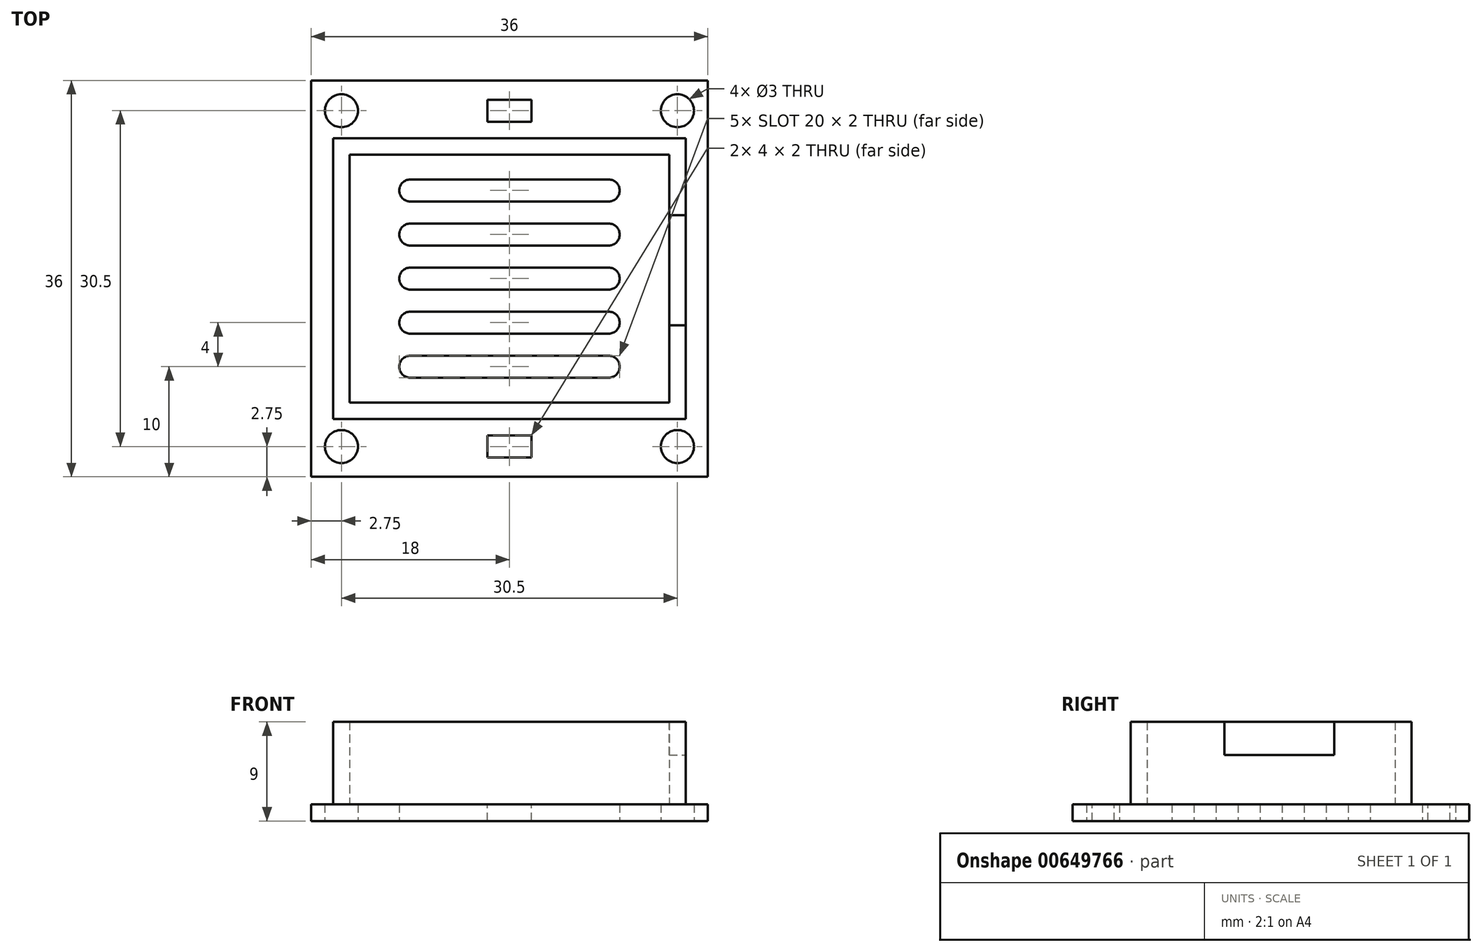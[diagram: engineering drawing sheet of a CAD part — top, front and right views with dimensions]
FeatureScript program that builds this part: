
annotation { "Feature Type Name" : "Feature", "Feature Type Description" : "" }
export const myFeature = defineFeature(function(context is Context, id is Id, definition is map)
    precondition{}
    {
        {
            var Q0;
            Q0=qCreatedBy(makeId("Top.planeOp"),FACE);
            var sketch = newSketch(context, id + "F0", { "sketchPlane" : qUnion([Q0])});
            skLineSegment(sketch, "E0.bottom", {"start": v(18, 18) * mm, "end": v(-18, 18) * mm});
            skLineSegment(sketch, "E0.top", {"start": v(18, -18) * mm, "end": v(-18, -18) * mm});
            skLineSegment(sketch, "E0.left", {"start": v(18, 18) * mm, "end": v(18, -18) * mm});
            skLineSegment(sketch, "E0.right", {"start": v(-18, 18) * mm, "end": v(-18, -18) * mm});
            skLineSegment(sketch, "E1.bottom", {"start": v(15.25, 15.25) * mm, "end": v(-15.25, 15.25) * mm, "construction": true});
            skLineSegment(sketch, "E1.top", {"start": v(15.25, -15.25) * mm, "end": v(-15.25, -15.25) * mm, "construction": true});
            skLineSegment(sketch, "E1.left", {"start": v(15.25, 15.25) * mm, "end": v(15.25, -15.25) * mm, "construction": true});
            skLineSegment(sketch, "E1.right", {"start": v(-15.25, 15.25) * mm, "end": v(-15.25, -15.25) * mm, "construction": true});
            skCircle(sketch, "E2", {"center": v(-15.25, 15.25) * mm, "radius": 1.5 * mm});
            skCircle(sketch, "E3", {"center": v(15.25, 15.25) * mm, "radius": 1.5 * mm});
            skCircle(sketch, "E4", {"center": v(15.25, -15.25) * mm, "radius": 1.5 * mm});
            skCircle(sketch, "E5", {"center": v(-15.25, -15.25) * mm, "radius": 1.5 * mm});
            skPoint(sketch, "E6.centerSnap0", {"position": v(15.25, 0) * mm});
            skSolve(sketch);
        }
        {
            var Q0;
            Q0=qCreatedBy(makeId("Top.planeOp"),FACE);
            var sketch = newSketch(context, id + "F1", { "sketchPlane" : qUnion([Q0])});
            skPoint(sketch, "E7.middle", {"position": v(0, 0) * mm});
            skLineSegment(sketch, "E8.bottom", {"start": v(-14.5, 11.25) * mm, "end": v(14.5, 11.25) * mm, "construction": true});
            skLineSegment(sketch, "E8.top", {"start": v(-14.5, -11.25) * mm, "end": v(14.5, -11.25) * mm, "construction": true});
            skLineSegment(sketch, "E8.left", {"start": v(-14.5, 11.25) * mm, "end": v(-14.5, -11.25) * mm, "construction": true});
            skLineSegment(sketch, "E8.right", {"start": v(14.5, 11.25) * mm, "end": v(14.5, -11.25) * mm, "construction": true});
            skLineSegment(sketch, "E9.bottom", {"start": v(-16, 12.75) * mm, "end": v(16, 12.75) * mm});
            skLineSegment(sketch, "E9.top", {"start": v(-16, -12.75) * mm, "end": v(16, -12.75) * mm});
            skLineSegment(sketch, "E9.left", {"start": v(-16, 12.75) * mm, "end": v(-16, -12.75) * mm});
            skLineSegment(sketch, "E9.right", {"start": v(16, 12.75) * mm, "end": v(16, -12.75) * mm});
            skSolve(sketch);
        }
        {
            var Q0;
            Q0=qCreatedBy(makeId("Top.planeOp"),FACE);
            var sketch = newSketch(context, id + "F2", { "sketchPlane" : qUnion([Q0])});
            skLineSegment(sketch, "E10.bottom", {"start": v(-9, 1) * mm, "end": v(9, 1) * mm});
            skLineSegment(sketch, "E10.top", {"start": v(-9, -1) * mm, "end": v(9, -1) * mm});
            skLineSegment(sketch, "E10.left", {"start": v(-9, 1) * mm, "end": v(-9, -1) * mm});
            skLineSegment(sketch, "E10.right", {"start": v(9, 1) * mm, "end": v(9, -1) * mm});
            skPoint(sketch, "E10.middle", {"position": v(0, 0) * mm});
            skCircle(sketch, "E11", {"center": v(-9, 0) * mm, "radius": 1 * mm});
            skCircle(sketch, "E12", {"center": v(9, 0) * mm, "radius": 1 * mm});
            skLineSegment(sketch, "E13.0.1.0", {"start": v(-9, 3) * mm, "end": v(9, 3) * mm});
            skLineSegment(sketch, "E13.0.1.1", {"start": v(-9, 5) * mm, "end": v(9, 5) * mm});
            skCircle(sketch, "E13.0.1.2", {"center": v(-9, 4) * mm, "radius": 1 * mm});
            skCircle(sketch, "E13.0.1.3", {"center": v(9, 4) * mm, "radius": 1 * mm});
            skPoint(sketch, "E13.0.1.4", {"position": v(0, 4) * mm});
            skLineSegment(sketch, "E13.0.1.5", {"start": v(9, 5) * mm, "end": v(9, 3) * mm});
            skLineSegment(sketch, "E13.0.1.6", {"start": v(-9, 5) * mm, "end": v(-9, 3) * mm});
            skLineSegment(sketch, "E13.0.2.0", {"start": v(-9, 7) * mm, "end": v(9, 7) * mm});
            skLineSegment(sketch, "E13.0.2.1", {"start": v(-9, 9) * mm, "end": v(9, 9) * mm});
            skCircle(sketch, "E13.0.2.2", {"center": v(-9, 8) * mm, "radius": 1 * mm});
            skCircle(sketch, "E13.0.2.3", {"center": v(9, 8) * mm, "radius": 1 * mm});
            skPoint(sketch, "E13.0.2.4", {"position": v(0, 8) * mm});
            skLineSegment(sketch, "E13.0.2.5", {"start": v(9, 9) * mm, "end": v(9, 7) * mm});
            skLineSegment(sketch, "E13.0.2.6", {"start": v(-9, 9) * mm, "end": v(-9, 7) * mm});
            skLineSegment(sketch, "E13.direction1", {"start": v(-9, -1) * mm, "end": v(16, -1) * mm, "construction": true});
            skLineSegment(sketch, "E13.direction2", {"start": v(-9, -1) * mm, "end": v(-9, 3) * mm, "construction": true});
            skCircle(sketch, "E14.0.1.0", {"center": v(9, -4) * mm, "radius": 1 * mm});
            skCircle(sketch, "E14.0.1.1", {"center": v(-9, -4) * mm, "radius": 1 * mm});
            skLineSegment(sketch, "E14.0.1.2", {"start": v(-9, -5) * mm, "end": v(9, -5) * mm});
            skLineSegment(sketch, "E14.0.1.3", {"start": v(-9, -3) * mm, "end": v(9, -3) * mm});
            skPoint(sketch, "E14.0.1.4", {"position": v(0, -4) * mm});
            skLineSegment(sketch, "E14.0.1.5", {"start": v(9, -3) * mm, "end": v(9, -5) * mm});
            skLineSegment(sketch, "E14.0.1.6", {"start": v(-9, -3) * mm, "end": v(-9, -5) * mm});
            skCircle(sketch, "E14.0.2.0", {"center": v(9, -8) * mm, "radius": 1 * mm});
            skCircle(sketch, "E14.0.2.1", {"center": v(-9, -8) * mm, "radius": 1 * mm});
            skLineSegment(sketch, "E14.0.2.2", {"start": v(-9, -9) * mm, "end": v(9, -9) * mm});
            skLineSegment(sketch, "E14.0.2.3", {"start": v(-9, -7) * mm, "end": v(9, -7) * mm});
            skPoint(sketch, "E14.0.2.4", {"position": v(0, -8) * mm});
            skLineSegment(sketch, "E14.0.2.5", {"start": v(9, -7) * mm, "end": v(9, -9) * mm});
            skLineSegment(sketch, "E14.0.2.6", {"start": v(-9, -7) * mm, "end": v(-9, -9) * mm});
            skLineSegment(sketch, "E14.direction2", {"start": v(-9, -1) * mm, "end": v(-9, -5) * mm, "construction": true});
            skSolve(sketch);
        }
        {
            var Q0;
            Q0 = qSketchRegion(id + "F0", true);
            extrude(context, id + "F3", {"entities" : qUnion([Q0]), "depth" : 1.5 * mm, "offsetDistance" : 25 * mm});
        }
        {
            var Q0;
            Q0 = qSketchRegion(id + "F1", true);
            extrude(context, id + "F4", {"entities" : qUnion([Q0]), "operationType" : NewBodyOperationType.ADD, "depth" : 9 * mm, "offsetDistance" : 25 * mm});
        }
        {
            var Q0;
            Q0=makeQuery(id+"F4.opExtrude","CAP_FACE",FACE,{"disambiguationData":[OSD([sQuery(id+"F1.wireOp",EDGE,"E9.bottom"),sQuery(id+"F1.wireOp",EDGE,"E9.top"),sQuery(id+"F1.wireOp",EDGE,"E9.left"),sQuery(id+"F1.wireOp",EDGE,"E9.right")])],"isStart":false});
            shell(context, id + "F5", {"entities" : qUnion([Q0]), "thickness" : 1.5 * mm});
        }
        {
            var Q0;
            Q0 = qSketchRegion(id + "F2", true);
            extrude(context, id + "F6", {"entities" : qUnion([Q0]), "operationType" : NewBodyOperationType.REMOVE, "depth" : 25 * mm, "offsetDistance" : 25 * mm});
        }
        {
            var Q0;
            Q0=makeQuery(id+"F4.opExtrude","CAP_FACE",FACE,{"disambiguationData":[OSD([sQuery(id+"F1.wireOp",EDGE,"E9.bottom"),sQuery(id+"F1.wireOp",EDGE,"E9.top"),sQuery(id+"F1.wireOp",EDGE,"E9.left"),sQuery(id+"F1.wireOp",EDGE,"E9.right")])],"isStart":false});
            var sketch = newSketch(context, id + "F7", { "sketchPlane" : qUnion([Q0])});
            skLineSegment(sketch, "E15.bottom", {"start": v(14.5, 5.75) * mm, "end": v(16, 5.75) * mm});
            skLineSegment(sketch, "E15.top", {"start": v(14.5, -4.25) * mm, "end": v(16, -4.25) * mm});
            skLineSegment(sketch, "E15.left", {"start": v(14.5, 5.75) * mm, "end": v(14.5, -4.25) * mm});
            skLineSegment(sketch, "E15.right", {"start": v(16, 5.75) * mm, "end": v(16, -4.25) * mm});
            skSolve(sketch);
        }
        {
            var Q0;
            Q0 = qSketchRegion(id + "F7", true);
            extrude(context, id + "F8", {"entities" : qUnion([Q0]), "operationType" : NewBodyOperationType.REMOVE, "oppositeDirection" : true, "depth" : 3 * mm, "offsetDistance" : 25 * mm});
        }
        {
            var Q0;
            Q0=makeQuery(id+"F3.opExtrude","CAP_FACE",FACE,{"disambiguationData":[OSD([sQuery(id+"F0.wireOp",EDGE,"E0.bottom"),sQuery(id+"F0.wireOp",EDGE,"E0.top"),sQuery(id+"F0.wireOp",EDGE,"E0.left"),sQuery(id+"F0.wireOp",EDGE,"E0.right"),sQuery(id+"F0.wireOp",EDGE,"E2"),sQuery(id+"F0.wireOp",EDGE,"E3"),sQuery(id+"F0.wireOp",EDGE,"E4"),sQuery(id+"F0.wireOp",EDGE,"E5")])],"isStart":false});
            var sketch = newSketch(context, id + "F9", { "sketchPlane" : qUnion([Q0])});
            skPoint(sketch, "E16.0", {"position": v(0, 15.25) * mm});
            skPoint(sketch, "E17.0", {"position": v(0, -15.25) * mm});
            skLineSegment(sketch, "E18.bottom", {"start": v(2, 14.25) * mm, "end": v(-2, 14.25) * mm});
            skLineSegment(sketch, "E18.top", {"start": v(2, 16.25) * mm, "end": v(-2, 16.25) * mm});
            skLineSegment(sketch, "E18.left", {"start": v(2, 14.25) * mm, "end": v(2, 16.25) * mm});
            skLineSegment(sketch, "E18.right", {"start": v(-2, 14.25) * mm, "end": v(-2, 16.25) * mm});
            skLineSegment(sketch, "E19.bottom", {"start": v(2, -16.25) * mm, "end": v(-2, -16.25) * mm});
            skLineSegment(sketch, "E19.top", {"start": v(2, -14.25) * mm, "end": v(-2, -14.25) * mm});
            skLineSegment(sketch, "E19.left", {"start": v(2, -16.25) * mm, "end": v(2, -14.25) * mm});
            skLineSegment(sketch, "E19.right", {"start": v(-2, -16.25) * mm, "end": v(-2, -14.25) * mm});
            skSolve(sketch);
        }
        {
            var Q0;
            Q0 = qSketchRegion(id + "F9", true);
            extrude(context, id + "F10", {"entities" : qUnion([Q0]), "operationType" : NewBodyOperationType.REMOVE, "oppositeDirection" : true, "depth" : 25 * mm, "offsetDistance" : 25 * mm});
        }
    });
